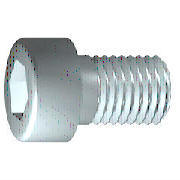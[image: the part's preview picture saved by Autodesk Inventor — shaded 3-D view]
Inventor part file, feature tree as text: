
AUTODESK INVENTOR PART (.ipt)
format: ipt  version: 2025.2 (Build 292293000, 293)  size: 196,096 bytes
history: native  units: mm (DEFAULTED — no unit token found)
features: other x1, extrude x1, chamfer x1, plane x1, fillet x1
ambient origin geometry x7: Origin, YZ Plane, XY Plane, X Axis, Y Axis, Z Axis, Center Point
bodies: Solid1 (feature_tree)
feature tree (5):
  other  "Körper"
  extrude  "Loch"  Depth=8.5mm
  chamfer  "Fase1"  Distance=0.306825mm
  plane  "Work Plane1"
  fillet  "Fillet2"  Radius=3.0mm
